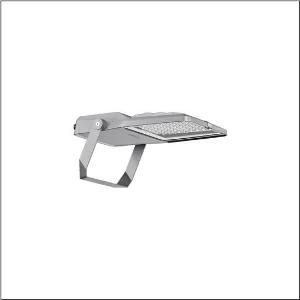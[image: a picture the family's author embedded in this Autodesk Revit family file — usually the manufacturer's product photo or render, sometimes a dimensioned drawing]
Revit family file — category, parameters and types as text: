
# Revit family: floodlight_fl_21_iq_mini___pl61_5xa7771c2c1a_d716
name_source: partatom
category: Lighting Fixtures
units: mm (PartAtom-declared; Revit-internal decimal feet)

## family parameters
Cut with Voids When Loaded = No
Host = Face
Light Source = No
Part Type = Normal
Room Calculation Point = No
Round Connector Dimension = Use Diameter
Shared = No

## types (1)
- --- (1 x LED, 11980 lm, 87.2 W, 3000K)
    Apparent Load = 87 VA
    CIE Flux Codes = 33 65 98 100 100
    Color Rendering = 70
    Color Temperature = 3000K
    Default Elevation = 1800 mm
    Description = Floodlight FL 21 iQ mini, floodlight, primary light control with lens, of PMMA, primary optical cover: protective disc, of toughened safety glass, transparent, light distribution: PL61, light emission: direct distribution, installation type: surface-mounted, LED, High Power LED, rated luminous flux: 11.980lm, luminous efficacy: 137lm/W, light colour: 730, colour temperature: 3000K, control: Auto-Match, Temp-Guard, Lumen-Switch, Night-Set, Smart-Wire, Light-Fading, Desk-Remote (wireless, voltage-free reading and setting of iQ features in the workshop via application-optimized NFC function/RFID function), optimised constant luminous flux control (CLO 2.0), with terminal, 6-pole, mains connection: 220..240V, AC, 50/60Hz, start of lifetime: 87W, end of service life: 92W, reduction: 40W, luminaire housing, of diecast aluminium, powder-coated, Siteco® metallic grey (DB 702S), corrosivity category C5 mid according to DIN EN ISO 12944, sealing non-destructively replaceable, mounting bracket, of steel, galvanised, powder-coated, Siteco® metallic grey (DB 702S), protection rating (complete): IP66, insulation class (complete): insulation class II (safety insulation), certification: CE, ENEC, VDE, protection symbol: D, impact resistance: IK08, permissible operating ambient temperature: -40..+40°C, permissible operating ambient temperature for outdoor applications: -40..+50°C, standard: DIN EN 12944, LABS conformity tested according to VDMA 24364:2018-05, packaging unit: 1 piece

Light Distribution: PL61
    Height = 70 mm
    Lamp = 1 x LED
    Lamp Light Flux = 11980 lm
    Lamp Power = 87.2 W
    Lamp count = 1
    Length = 485 mm
    Luminous efficacy = 137 lm/W
    Manufacturer = Siteco
    ModVariant = No
    Model = 5XA7771C2C1A
    Number of Poles = 1
    OnlyDefault = Yes
    Power Factor = 1
    Product Name = Floodlight FL 21 iQ mini | PL61
    Product group = floodlight | pylon annexe
    ProductGroupID = 6200
    Protection Class = Protection class II
    Protection Degree = IP 66
    RLX_Detail_Level = 1
    RLX_Emergency_Light_Flux = 0 lm
    RLX_Emergency_Type = 0
    RLX_Emergency_Type_DB = No
    RlxData = <blob elided: 96389 chars, md5=f1302efe>
    Socket = socket
    Standby Power = 0 W
    System Light Flux = 11980 lm
    System Power = 87 W
    Type Comments = factory setting: luminous flux: 100 % | dim-lin: 254 | 456 mA
    Type Image = l_1006845.jpg
    URL = http://relux.com
    VarID = @adj_106443
    Voltage = 0 V
    Weight = 0.00 kg
    Width = 337 mm

## geometry (parser evidence)
native form markers: Blend x4, Sweep x10
no freeform markers — native parametric forms only
